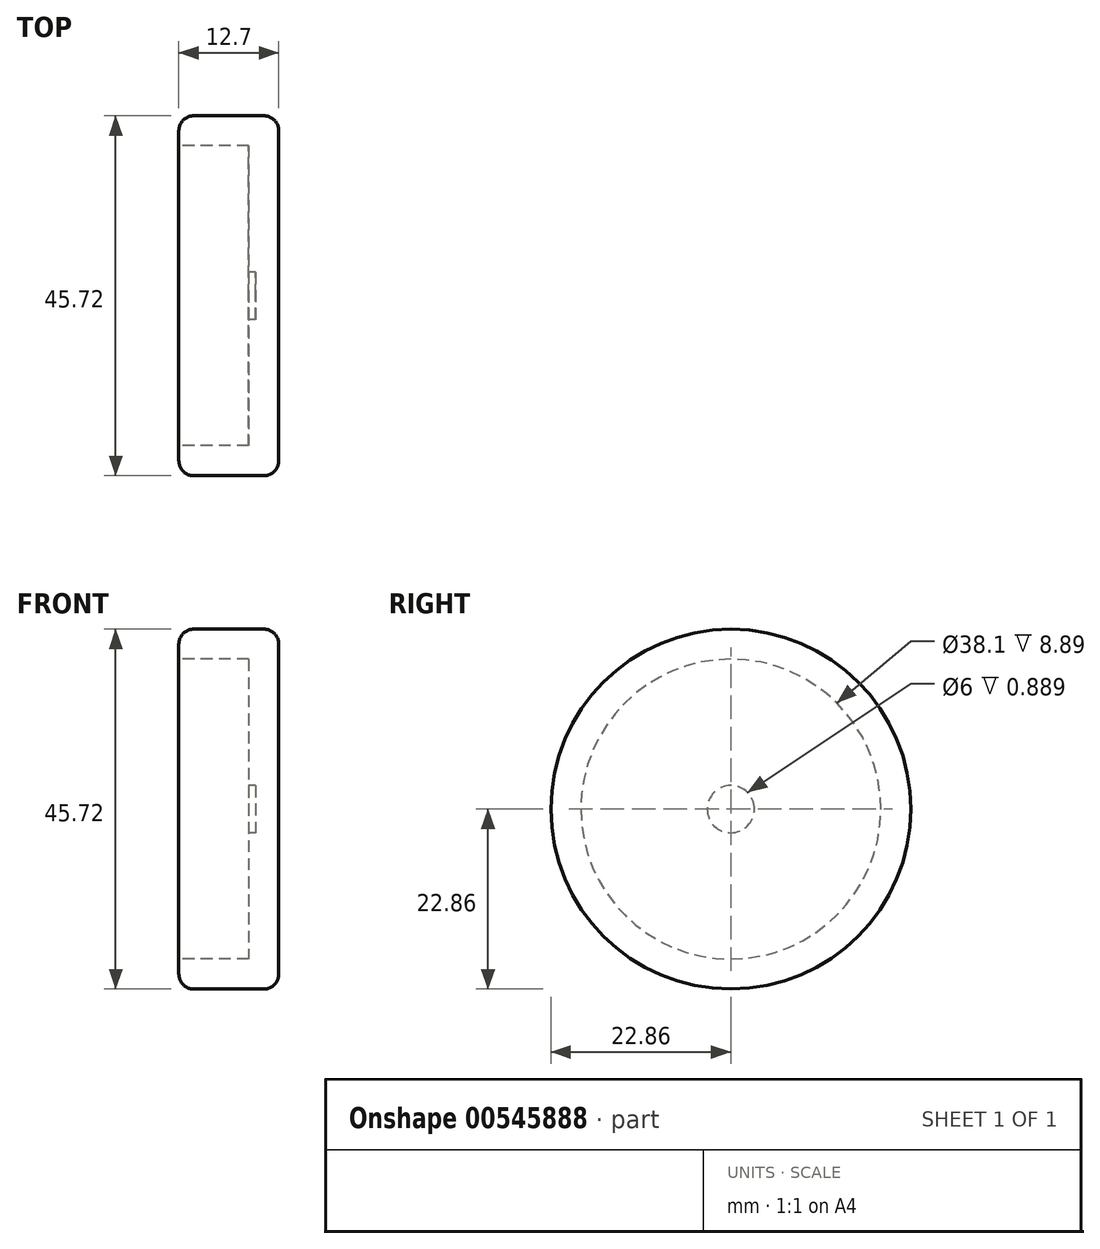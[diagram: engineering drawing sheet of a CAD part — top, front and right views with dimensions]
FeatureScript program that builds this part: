
annotation { "Feature Type Name" : "Feature", "Feature Type Description" : "" }
export const myFeature = defineFeature(function(context is Context, id is Id, definition is map)
    precondition{}
    {
        {
            var Q0;
            Q0=qCreatedBy(makeId("Front.planeOp"),FACE);
            var sketch = newSketch(context, id + "F0", { "sketchPlane" : qUnion([Q0])});
            skLineSegment(sketch, "E0", {"start": v(0, 19.05) * mm, "end": v(8.89, 19.05) * mm});
            skLineSegment(sketch, "E1", {"start": v(8.9, 19.05) * mm, "end": v(8.9, 0) * mm});
            skLineSegment(sketch, "E2", {"start": v(8.9, 0) * mm, "end": v(12.7, 0) * mm});
            skLineSegment(sketch, "E3", {"start": v(12.7, 0) * mm, "end": v(12.7, 20.96) * mm});
            skLineSegment(sketch, "E4", {"start": v(10.8, 22.86) * mm, "end": v(1.9, 22.86) * mm});
            skLineSegment(sketch, "E5", {"start": v(0, 20.96) * mm, "end": v(0, 19.05) * mm});
            skPoint(sketch, "E6.visualSharp", {"position": v(12.7, 22.86) * mm});
            skArc(sketch, "E6.filletArc", {"start": v(12.7, 20.96) * mm, "mid": v(12.14, 22.3) * mm, "end": v(10.8, 22.86) * mm});
            skPoint(sketch, "E7.visualSharp", {"position": v(0, 22.86) * mm});
            skArc(sketch, "E7.filletArc", {"start": v(1.9, 22.86) * mm, "mid": v(0.56, 22.3) * mm, "end": v(0, 20.96) * mm});
            skLineSegment(sketch, "E8", {"start": v(-7.84, 0) * mm, "end": v(12.7, 0) * mm, "construction": true});
            skSolve(sketch);
        }
        {
            var Q0;
            Q0 = qSketchRegion(id + "F0", true);
            var Q1;
            Q1=sQuery(id+"F0.wireOp",EDGE,"E8");
            revolve(context, id + "F1", {"surfaceOperationType" : NewSurfaceOperationType.NEW, "entities" : qUnion([Q0]), "axis" : qUnion([Q1]), "revolveType" : RevolveType.FULL});
        }
        {
            var Q0;
            Q0=makeQuery(id+"F1.opRevolve","SWEPT_FACE",FACE,{"disambiguationData":[OSD([sQuery(id+"F0.wireOp",EDGE,"E1")])]});
            var sketch = newSketch(context, id + "F2", { "sketchPlane" : qUnion([Q0])});
            skCircle(sketch, "E9", {"center": v(0, 0) * mm, "radius": 3 * mm});
            skSolve(sketch);
        }
        {
            var Q0;
            Q0 = qSketchRegion(id + "F2", true);
            extrude(context, id + "F3", {"entities" : qUnion([Q0]), "operationType" : NewBodyOperationType.REMOVE, "oppositeDirection" : true, "depth" : 0.89 * mm, "offsetDistance" : 25.4 * mm});
        }
    });
